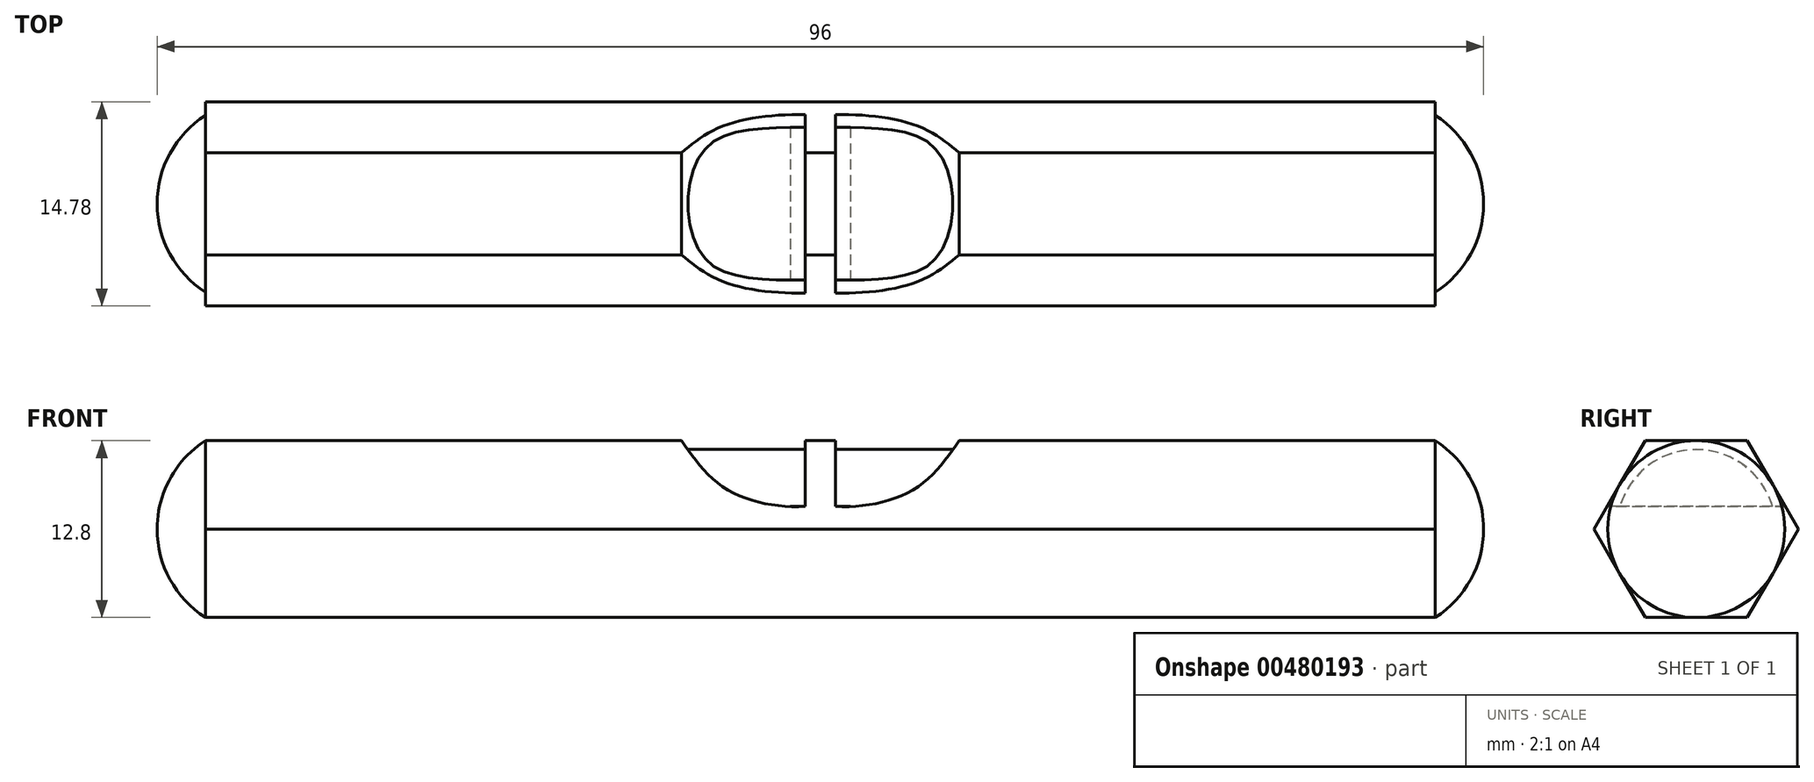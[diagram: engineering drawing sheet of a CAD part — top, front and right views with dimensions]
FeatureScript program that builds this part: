
annotation { "Feature Type Name" : "Feature", "Feature Type Description" : "" }
export const myFeature = defineFeature(function(context is Context, id is Id, definition is map)
    precondition{}
    {
        {
            var Q0;
            Q0=qCreatedBy(makeId("Right.planeOp"),FACE);
            var sketch = newSketch(context, id + "F0", { "sketchPlane" : qUnion([Q0])});
            skPoint(sketch, "E0.center.orphan", {"position": v(1.18, 0) * mm});
            skCircle(sketch, "E1", {"center": v(0, 0) * mm, "radius": 6.4 * mm});
            skCircle(sketch, "E2.cCircle", {"center": v(0, 0) * mm, "radius": 6.4 * mm, "construction": true});
            skLineSegment(sketch, "E2.0", {"start": v(-3.7, 6.4) * mm, "end": v(3.7, 6.4) * mm});
            skLineSegment(sketch, "E2.1", {"start": v(3.7, 6.4) * mm, "end": v(7.4, 0) * mm});
            skLineSegment(sketch, "E2.2", {"start": v(7.4, 0) * mm, "end": v(3.7, -6.4) * mm});
            skLineSegment(sketch, "E2.3", {"start": v(3.7, -6.4) * mm, "end": v(-3.7, -6.4) * mm});
            skLineSegment(sketch, "E2.4", {"start": v(-3.7, -6.4) * mm, "end": v(-7.4, 0) * mm});
            skLineSegment(sketch, "E2.5", {"start": v(-7.4, 0) * mm, "end": v(-3.7, 6.4) * mm});
            skPoint(sketch, "E2.0.midPoint", {"position": v(0, 6.4) * mm});
            skSolve(sketch);
        }
        {
            var Q0;
            {var subQ0=sQuery(id+"F0.wireOp",EDGE,"E2.0");var subQ1=sQuery(id+"F0.wireOp",EDGE,"E1");var subQ2=makeQuery(id+"F0.imprint","INTERSECT",VERTEX,{"derivedFrom":[subQ1,subQ0]});Q0=makeQuery(id+"F0.imprint","IMPRINT",FACE,{"disambiguationData":[TD([[makeQuery(id+"F0.imprint","IMPRINT",EDGE,{"disambiguationData":[TD([[subQ2,1.0]])],"derivedFrom":subQ1}),-1.0]])]});}
            var Q1;
            {var subQ0=sQuery(id+"F0.wireOp",EDGE,"E2.0");var subQ1=sQuery(id+"F0.wireOp",EDGE,"E1");var subQ2=makeQuery(id+"F0.imprint","INTERSECT",VERTEX,{"derivedFrom":[subQ1,subQ0]});Q1=makeQuery(id+"F0.imprint","IMPRINT",FACE,{"disambiguationData":[TD([[makeQuery(id+"F0.imprint","IMPRINT",EDGE,{"disambiguationData":[TD([[subQ2,-1.0]])],"derivedFrom":subQ1}),-1.0]])]});}
            var Q2;
            {var subQ0=sQuery(id+"F0.wireOp",EDGE,"E2.5");var subQ1=sQuery(id+"F0.wireOp",EDGE,"E1");var subQ2=makeQuery(id+"F0.imprint","INTERSECT",VERTEX,{"derivedFrom":[subQ1,subQ0]});Q2=makeQuery(id+"F0.imprint","IMPRINT",FACE,{"disambiguationData":[TD([[makeQuery(id+"F0.imprint","IMPRINT",EDGE,{"disambiguationData":[TD([[subQ2,-1.0]])],"derivedFrom":subQ1}),-1.0]])]});}
            var Q3;
            {var subQ0=sQuery(id+"F0.wireOp",EDGE,"E2.4");var subQ1=sQuery(id+"F0.wireOp",EDGE,"E1");var subQ2=makeQuery(id+"F0.imprint","INTERSECT",VERTEX,{"derivedFrom":[subQ1,subQ0]});Q3=makeQuery(id+"F0.imprint","IMPRINT",FACE,{"disambiguationData":[TD([[makeQuery(id+"F0.imprint","IMPRINT",EDGE,{"disambiguationData":[TD([[subQ2,-1.0]])],"derivedFrom":subQ1}),-1.0]])]});}
            var Q4;
            {var subQ0=sQuery(id+"F0.wireOp",EDGE,"E2.3");var subQ1=sQuery(id+"F0.wireOp",EDGE,"E1");var subQ2=makeQuery(id+"F0.imprint","INTERSECT",VERTEX,{"derivedFrom":[subQ1,subQ0]});Q4=makeQuery(id+"F0.imprint","IMPRINT",FACE,{"disambiguationData":[TD([[makeQuery(id+"F0.imprint","IMPRINT",EDGE,{"disambiguationData":[TD([[subQ2,-1.0]])],"derivedFrom":subQ1}),-1.0]])]});}
            var Q5;
            {var subQ0=sQuery(id+"F0.wireOp",EDGE,"E2.1");var subQ1=sQuery(id+"F0.wireOp",EDGE,"E1");var subQ2=makeQuery(id+"F0.imprint","INTERSECT",VERTEX,{"derivedFrom":[subQ1,subQ0]});Q5=makeQuery(id+"F0.imprint","IMPRINT",FACE,{"disambiguationData":[TD([[makeQuery(id+"F0.imprint","IMPRINT",EDGE,{"disambiguationData":[TD([[subQ2,1.0]])],"derivedFrom":subQ1}),-1.0]])]});}
            var Q6;
            {var subQ0=sQuery(id+"F0.wireOp",EDGE,"E1");var subQ4=makeQuery(id+"F0.imprint","INTERSECT",VERTEX,{"derivedFrom":[subQ0,sQuery(id+"F0.wireOp",EDGE,"E2.0")]});Q6=makeQuery(id+"F0.imprint","IMPRINT",FACE,{"disambiguationData":[TD([[makeQuery(id+"F0.imprint","IMPRINT",EDGE,{"disambiguationData":[TD([[subQ4,1.0]])],"derivedFrom":subQ0}),1.0]])]});}
            extrude(context, id + "F1", {"entities" : qUnion([Q0, Q1, Q2, Q3, Q4, Q5, Q6]), "depth" : 89 * mm});
        }
        {
            var Q0;
            Q0=qCreatedBy(makeId("Top.planeOp"),FACE);
            var sketch = newSketch(context, id + "F2", { "sketchPlane" : qUnion([Q0])});
            skLineSegment(sketch, "E3", {"start": v(0, 0) * mm, "end": v(-3.5, 0) * mm, "construction": true});
            skSolve(sketch);
        }
        {
            var Q0;
            Q0=qCreatedBy(makeId("Front.planeOp"),FACE);
            var sketch = newSketch(context, id + "F3", { "sketchPlane" : qUnion([Q0])});
            skArc(sketch, "E4", {"start": v(0, 6.4) * mm, "mid": v(-2.57, 3.65) * mm, "end": v(-3.5, 0) * mm});
            skLineSegment(sketch, "E5", {"start": v(0, 6.4) * mm, "end": v(0, 0) * mm});
            skLineSegment(sketch, "E6", {"start": v(0, 0) * mm, "end": v(-3.5, 0) * mm});
            skPoint(sketch, "E7.orphan", {"position": v(0, -6.4) * mm});
            skSolve(sketch);
        }
        {
            var Q0;
            Q0=makeQuery(id+"F3.imprint","IMPRINT",FACE,{"disambiguationData":[TD([[makeQuery(id+"F3.imprint","IMPRINT",EDGE,{"derivedFrom":sQuery(id+"F3.wireOp",EDGE,"E4")}),1.0]])]});
            var Q1;
            Q1=sQuery(id+"F3.wireOp",EDGE,"E6");
            revolve(context, id + "F4", {"operationType" : NewBodyOperationType.ADD, "surfaceOperationType" : NewSurfaceOperationType.NEW, "entities" : qUnion([Q0]), "axis" : qUnion([Q1]), "revolveType" : RevolveType.FULL});
        }
        {
            var Q0;
            Q0=makeQuery(id+"F1.opExtrude","SWEPT_BODY",BODY,{"disambiguationData":[OSD([sQuery(id+"F0.wireOp",EDGE,"E2.0"),sQuery(id+"F0.wireOp",EDGE,"E2.1"),sQuery(id+"F0.wireOp",EDGE,"E2.2"),sQuery(id+"F0.wireOp",EDGE,"E2.3"),sQuery(id+"F0.wireOp",EDGE,"E2.4"),sQuery(id+"F0.wireOp",EDGE,"E2.5")])]});
            transform(context, id + "F5", {"entities" : qUnion([Q0]), "transformType" : TransformType.TRANSLATION_3D, "dx" : -44.5 * mm, "dy" : 0 * mm, "dz" : 0 * mm, "makeCopy" : false});
        }
        {
            var Q0;
            Q0=makeQuery(id+"F1.opExtrude","SWEPT_BODY",BODY,{"disambiguationData":[OSD([sQuery(id+"F0.wireOp",EDGE,"E2.0"),sQuery(id+"F0.wireOp",EDGE,"E2.1"),sQuery(id+"F0.wireOp",EDGE,"E2.2"),sQuery(id+"F0.wireOp",EDGE,"E2.3"),sQuery(id+"F0.wireOp",EDGE,"E2.4"),sQuery(id+"F0.wireOp",EDGE,"E2.5")])]});
            var Q1;
            Q1=qCreatedBy(makeId("Right.planeOp"),FACE);
            mirror(context, id + "F6", {"operationType" : NewBodyOperationType.ADD, "entities" : qUnion([Q0]), "mirrorPlane" : qUnion([Q1])});
        }
        {
            var Q0;
            Q0=qCreatedBy(makeId("Front.planeOp"),FACE);
            var sketch = newSketch(context, id + "F7", { "sketchPlane" : qUnion([Q0])});
            skLineSegment(sketch, "E8", {"start": v(-1.08, 6.98) * mm, "end": v(-1.08, 6.4) * mm, "construction": true});
            skLineSegment(sketch, "E9", {"start": v(-1.08, 6.4) * mm, "end": v(-10.05, 6.4) * mm});
            skFitSpline(sketch, "E10", {"points": [v(-10.05, 6.4) * mm, v(-7.78, 3.62) * mm, v(-4.82, 2.05) * mm, v(-1.08, 1.63) * mm], "startDerivative": vector(6.1, -8.82) * mm, "endDerivative": vector(10.44, 0.49) * mm});
            skLineSegment(sketch, "E11", {"start": v(-1.08, 6.4) * mm, "end": v(-1.08, 1.63) * mm});
            skLineSegment(sketch, "E12.MirrorCS", {"start": v(1.08, 6.98) * mm, "end": v(1.08, 6.4) * mm, "construction": true});
            skLineSegment(sketch, "E13.MirrorCS", {"start": v(1.08, 6.4) * mm, "end": v(10.05, 6.4) * mm});
            skFitSpline(sketch, "E14.MirrorCS", {"points": [v(10.05, 6.4) * mm, v(7.78, 3.62) * mm, v(4.82, 2.05) * mm, v(1.08, 1.63) * mm], "startDerivative": vector(-6.1, -8.82) * mm, "endDerivative": vector(-10.44, 0.49) * mm});
            skLineSegment(sketch, "E15.MirrorCS", {"start": v(1.08, 6.4) * mm, "end": v(1.08, 1.63) * mm});
            skSolve(sketch);
        }
        {
            var Q0;
            Q0 = qSketchRegion(id + "F7", true);
            extrude(context, id + "F8", {"entities" : qUnion([Q0]), "operationType" : NewBodyOperationType.REMOVE, "endBound" : BoundingType.SYMMETRIC, "oppositeDirection" : true, "depth" : 25 * mm});
        }
        {
            var Q0;
            Q0=makeQuery(id+"F8.boolean.opBoolean","COPY",FACE,{"derivedFrom":makeQuery(id+"F8.opExtrude","SWEPT_FACE",FACE,{"disambiguationData":[OSD([sQuery(id+"F7.wireOp",EDGE,"E15.MirrorCS")])]})});
            var sketch = newSketch(context, id + "F9", { "sketchPlane" : qUnion([Q0])});
            skCircle(sketch, "E16", {"center": v(0, 0) * mm, "radius": 5.76 * mm});
            skSolve(sketch);
        }
        {
            var Q0;
            {var subQ0=sQuery(id+"F9.wireOp",EDGE,"E16");var subQ1=makeQuery(id+"F8.boolean.opBoolean","COPY",EDGE,{"derivedFrom":makeQuery(id+"F8.opExtrude","SWEPT_EDGE",EDGE,{"disambiguationData":[OSD([sQuery(id+"F7.wireOp",EDGE,"E14.MirrorCS"),sQuery(id+"F7.wireOp",EDGE,"E15.MirrorCS")])]})});var subQ2=makeQuery(id+"F9.imprint","INTERSECT",VERTEX,{"disambiguationData":[OD(0.0)],"derivedFrom":[subQ1,subQ0]});Q0=makeQuery(id+"F9.imprint","IMPRINT",FACE,{"disambiguationData":[TD([[makeQuery(id+"F9.imprint","IMPRINT",EDGE,{"disambiguationData":[TD([[subQ2,-1.0]])],"derivedFrom":subQ0}),1.0]])]});}
            extrude(context, id + "F10", {"entities" : qUnion([Q0]), "operationType" : NewBodyOperationType.ADD, "endBound" : BoundingType.SYMMETRIC, "depth" : 25 * mm});
        }
    });
